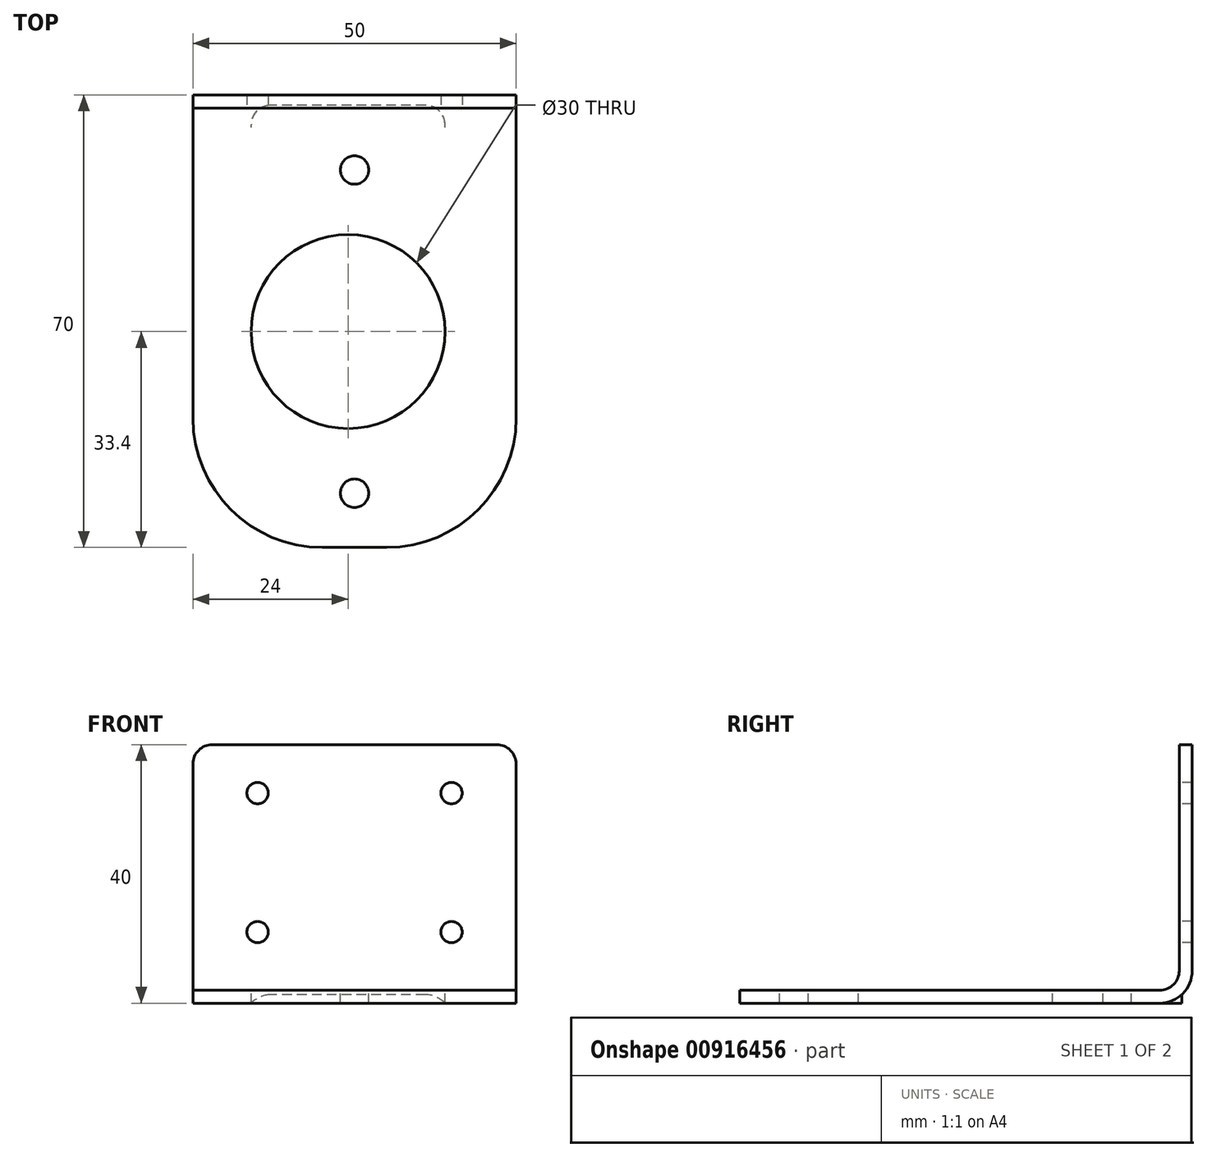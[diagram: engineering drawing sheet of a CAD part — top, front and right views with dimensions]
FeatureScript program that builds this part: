
annotation { "Feature Type Name" : "Feature", "Feature Type Description" : "" }
export const myFeature = defineFeature(function(context is Context, id is Id, definition is map)
    precondition{}
    {
        {
            var Q0;
            Q0=qCreatedBy(makeId("Right.planeOp"),FACE);
            var sketch = newSketch(context, id + "F0", { "sketchPlane" : qUnion([Q0])});
            skLineSegment(sketch, "E0", {"start": v(0, 5) * mm, "end": v(0, 40) * mm});
            skLineSegment(sketch, "E1", {"start": v(-5, 0) * mm, "end": v(-70, 0) * mm});
            skPoint(sketch, "E2.visualSharp", {"position": v(0, 0) * mm});
            skArc(sketch, "E2.filletArc", {"start": v(-5, 0) * mm, "mid": v(-1.46, 1.46) * mm, "end": v(0, 5) * mm});
            skLineSegment(sketch, "E3.0", {"start": v(-2, 5) * mm, "end": v(-2, 40) * mm});
            skArc(sketch, "E3.1", {"start": v(-5, 2) * mm, "mid": v(-2.88, 2.88) * mm, "end": v(-2, 5) * mm});
            skLineSegment(sketch, "E3.2", {"start": v(-5, 2) * mm, "end": v(-70, 2) * mm});
            skLineSegment(sketch, "E4", {"start": v(-70, 2) * mm, "end": v(-70, 0) * mm});
            skLineSegment(sketch, "E5", {"start": v(-2, 40) * mm, "end": v(0, 40) * mm});
            skSolve(sketch);
        }
        {
            var Q0;
            Q0=makeQuery(id+"F0.imprint","IMPRINT",FACE,{"disambiguationData":[TD([[makeQuery(id+"F0.imprint","IMPRINT",EDGE,{"derivedFrom":sQuery(id+"F0.wireOp",EDGE,"E0")}),1.0]])]});
            extrude(context, id + "F1", {"entities" : qUnion([Q0]), "endBound" : BoundingType.SYMMETRIC, "depth" : 50 * mm});
        }
        {
            var Q0;
            Q0=makeQuery(id+"F1.opExtrude","SWEPT_FACE",FACE,{"disambiguationData":[OSD([sQuery(id+"F0.wireOp",EDGE,"E3.0")])]});
            var sketch = newSketch(context, id + "F2", { "sketchPlane" : qUnion([Q0])});
            skLineSegment(sketch, "E6.bottom", {"start": v(15, 32.5) * mm, "end": v(-15, 32.5) * mm});
            skLineSegment(sketch, "E6.top", {"start": v(15, 11) * mm, "end": v(-15, 11) * mm});
            skLineSegment(sketch, "E6.left", {"start": v(15, 32.5) * mm, "end": v(15, 11) * mm});
            skLineSegment(sketch, "E6.right", {"start": v(-15, 32.5) * mm, "end": v(-15, 11) * mm});
            skPoint(sketch, "E6.middle", {"position": v(0, 21.75) * mm});
            skSolve(sketch);
        }
        {
            var Q0;
            Q0=sQuery(id+"F2.wireOp",VERTEX,"E6.right.start");
            var Q1;
            Q1=sQuery(id+"F2.wireOp",VERTEX,"E6.top.end");
            var Q2;
            Q2=sQuery(id+"F2.wireOp",VERTEX,"E6.left.end");
            var Q3;
            Q3=sQuery(id+"F2.wireOp",VERTEX,"E6.left.start");
            var Q4;
            Q4=makeQuery(id+"F1.opExtrude","SWEPT_BODY",BODY,{"disambiguationData":[OSD([sQuery(id+"F0.wireOp",EDGE,"E0"),sQuery(id+"F0.wireOp",EDGE,"E1"),sQuery(id+"F0.wireOp",EDGE,"E2.filletArc"),sQuery(id+"F0.wireOp",EDGE,"E3.0"),sQuery(id+"F0.wireOp",EDGE,"E3.1"),sQuery(id+"F0.wireOp",EDGE,"E3.2"),sQuery(id+"F0.wireOp",EDGE,"E4"),sQuery(id+"F0.wireOp",EDGE,"E5")])]});
            hole(context, id + "F3", {"style" : HoleStyle.SIMPLE, "endStyle" : HoleEndStyle.THROUGH, "standardTappedOrClearance" : lookupTablePath({ "standard" : "ISO", "fit" : "Normal", "size" : "M3", "type" : "Clearance" }), "standardBlindInLast" : lookupTablePath({ "fit" : "Standard", "standard" : "ISO", "size" : "M3", "type" : "Clearance" }), "holeDiameter" : 3.3 * mm, "tappedDepth" : 12 * mm, "tapClearance" : 3, "locations" : qUnion([Q0, Q1, Q2, Q3]), "scope" : qUnion([Q4])});
        }
        {
            var Q0;
            Q0=makeQuery(id+"F1.opExtrude","SWEPT_FACE",FACE,{"disambiguationData":[OSD([sQuery(id+"F0.wireOp",EDGE,"E3.2")])]});
            var sketch = newSketch(context, id + "F4", { "sketchPlane" : qUnion([Q0])});
            skLineSegment(sketch, "E7.bottom", {"start": v(14, -61.6) * mm, "end": v(14, -71.6) * mm});
            skLineSegment(sketch, "E7.top", {"start": v(-16, -61.6) * mm, "end": v(-16, -71.6) * mm});
            skLineSegment(sketch, "E7.left", {"start": v(14, -61.6) * mm, "end": v(-16, -61.6) * mm});
            skLineSegment(sketch, "E7.right", {"start": v(14, -68.4) * mm, "end": v(-16, -68.4) * mm});
            skLineSegment(sketch, "E8", {"start": v(0, -61.6) * mm, "end": v(0, -71.6) * mm, "construction": true});
            skLineSegment(sketch, "E9.MirrorCS", {"start": v(14, -11.6) * mm, "end": v(14, -1.6) * mm});
            skLineSegment(sketch, "E10.MirrorCS", {"start": v(-16, -11.6) * mm, "end": v(-16, -1.6) * mm});
            skLineSegment(sketch, "E11.MirrorCS", {"start": v(14, -11.6) * mm, "end": v(-16, -11.6) * mm});
            skLineSegment(sketch, "E12.MirrorCS", {"start": v(14, -1.6) * mm, "end": v(-16, -1.6) * mm});
            skLineSegment(sketch, "E13.MirrorCS", {"start": v(0, -11.6) * mm, "end": v(0, -1.6) * mm, "construction": true});
            skCircle(sketch, "E14", {"center": v(-1, -36.6) * mm, "radius": 15 * mm});
            skLineSegment(sketch, "E15", {"start": v(0, -21.63) * mm, "end": v(25, -21.63) * mm});
            skLineSegment(sketch, "E16", {"start": v(0, -51.57) * mm, "end": v(25, -51.57) * mm});
            skSolve(sketch);
        }
        {
            var Q0;
            Q0=makeQuery(id+"F4.imprint","IMPRINT",FACE,{"disambiguationData":[TD([[makeQuery(id+"F4.imprint","IMPRINT",EDGE,{"derivedFrom":sQuery(id+"F4.wireOp",EDGE,"E7.bottom")}),-1.0]])]});
            var Q1;
            Q1=makeQuery(id+"F4.imprint","IMPRINT",FACE,{"disambiguationData":[TD([[makeQuery(id+"F4.imprint","IMPRINT",EDGE,{"derivedFrom":sQuery(id+"F4.wireOp",EDGE,"E9.MirrorCS")}),1.0]])]});
            var Q2;
            Q2=makeQuery(id+"F1.opExtrude","SWEPT_FACE",FACE,{"disambiguationData":[OSD([sQuery(id+"F0.wireOp",EDGE,"E1")])]});
            extrude(context, id + "F5", {"entities" : qUnion([Q0, Q1]), "operationType" : NewBodyOperationType.ADD, "endBound" : BoundingType.UP_TO_SURFACE, "oppositeDirection" : true, "endBoundEntityFace" : qUnion([Q2]), "depth" : 25 * mm});
        }
        {
            var Q0;
            Q0=sQuery(id+"F4.wireOp",VERTEX,"E8.start");
            var Q1;
            Q1=sQuery(id+"F4.wireOp",VERTEX,"E13.MirrorCS.start");
            var Q2;
            Q2=makeQuery(id+"F1.opExtrude","SWEPT_BODY",BODY,{"disambiguationData":[OSD([sQuery(id+"F0.wireOp",EDGE,"E0"),sQuery(id+"F0.wireOp",EDGE,"E1"),sQuery(id+"F0.wireOp",EDGE,"E2.filletArc"),sQuery(id+"F0.wireOp",EDGE,"E3.0"),sQuery(id+"F0.wireOp",EDGE,"E3.1"),sQuery(id+"F0.wireOp",EDGE,"E3.2"),sQuery(id+"F0.wireOp",EDGE,"E4"),sQuery(id+"F0.wireOp",EDGE,"E5")])]});
            hole(context, id + "F6", {"style" : HoleStyle.SIMPLE, "endStyle" : HoleEndStyle.THROUGH, "standardTappedOrClearance" : lookupTablePath({ "standard" : "ISO", "fit" : "Normal", "size" : "M4", "type" : "Clearance" }), "standardBlindInLast" : lookupTablePath({ "fit" : "Standard", "standard" : "ISO", "size" : "M4", "type" : "Clearance" }), "holeDiameter" : 4.4 * mm, "tappedDepth" : 12 * mm, "tapClearance" : 3, "locations" : qUnion([Q0, Q1]), "scope" : qUnion([Q2])});
        }
        {
            var Q0;
            {var subQ0=sQuery(id+"F4.wireOp",EDGE,"hzME8n18-MPXb-ktXV-Iea0-p6DPRJ7Zrk4K");Q0=makeQuery(id+"F4.imprint","IMPRINT",FACE,{"disambiguationData":[TD([[makeQuery(id+"F4.imprint","IMPRINT",EDGE,{"derivedFrom":subQ0}),1.0]])]});}
            var Q1;
            {var subQ0=sQuery(id+"F4.wireOp",EDGE,"ZWVXp8VA-qsCd-atnR-KfRt-9iqPWuk9H4GU");Q1=makeQuery(id+"F4.imprint","IMPRINT",FACE,{"disambiguationData":[TD([[makeQuery(id+"F4.imprint","IMPRINT",EDGE,{"derivedFrom":subQ0}),-1.0]])]});}
            var Q2;
            {var subQ0=sQuery(id+"F4.wireOp",EDGE,"E14");var subQ1=makeQuery(id+"F4.imprint","INTERSECT",VERTEX,{"derivedFrom":[subQ0,sQuery(id+"F4.wireOp",EDGE,"E15")]});Q2=makeQuery(id+"F4.imprint","IMPRINT",FACE,{"disambiguationData":[TD([[makeQuery(id+"F4.imprint","IMPRINT",EDGE,{"disambiguationData":[TD([[subQ1,1.0]])],"derivedFrom":subQ0}),1.0]])]});}
            extrude(context, id + "F7", {"entities" : qUnion([Q0, Q1, Q2]), "operationType" : NewBodyOperationType.REMOVE, "endBound" : BoundingType.UP_TO_NEXT, "oppositeDirection" : true, "offsetDistance" : 25 * mm, "depth" : 25 * mm});
        }
        {
            var Q0;
            Q0=makeQuery(id+"F7.boolean.opBoolean","COPY",EDGE,{"derivedFrom":makeQuery(id+"F7.opExtrude","SWEPT_EDGE",EDGE,{"disambiguationData":[OSD([sQuery(id+"F0.wireOp",EDGE,"E3.2"),sQuery(id+"F0.wireOp",EDGE,"E4"),sQuery(id+"F4.wireOp",EDGE,"hzME8n18-MPXb-ktXV-Iea0-p6DPRJ7Zrk4K")])]})});
            var Q1;
            Q1=makeQuery(id+"F5.opExtrude","SWEPT_EDGE",EDGE,{"disambiguationData":[OSD([sQuery(id+"F4.wireOp",EDGE,"E7.bottom"),sQuery(id+"F4.wireOp",EDGE,"E7.right")])]});
            var Q2;
            Q2=makeQuery(id+"F5.opExtrude","SWEPT_EDGE",EDGE,{"disambiguationData":[OSD([sQuery(id+"F4.wireOp",EDGE,"E7.top"),sQuery(id+"F4.wireOp",EDGE,"E7.right")])]});
            var Q3;
            Q3=makeQuery(id+"F5.opExtrude","SWEPT_EDGE",EDGE,{"disambiguationData":[OSD([sQuery(id+"F0.wireOp",EDGE,"E3.2"),sQuery(id+"F4.wireOp",EDGE,"E7.top"),sQuery(id+"F4.wireOp",EDGE,"E7.left")])]});
            var Q4;
            Q4=makeQuery(id+"F1.opExtrude","CAP_EDGE",EDGE,{"disambiguationData":[OSD([sQuery(id+"F0.wireOp",EDGE,"E5")])],"isStart":true});
            var Q5;
            Q5=makeQuery(id+"F7.boolean.opBoolean","COPY",EDGE,{"derivedFrom":makeQuery(id+"F7.opExtrude","SWEPT_EDGE",EDGE,{"disambiguationData":[OSD([sQuery(id+"F0.wireOp",EDGE,"E3.2"),sQuery(id+"F0.wireOp",EDGE,"E4"),sQuery(id+"F4.wireOp",EDGE,"ZWVXp8VA-qsCd-atnR-KfRt-9iqPWuk9H4GU")])]})});
            var Q6;
            Q6=makeQuery(id+"F5.opExtrude","SWEPT_EDGE",EDGE,{"disambiguationData":[OSD([sQuery(id+"F4.wireOp",EDGE,"E9.MirrorCS"),sQuery(id+"F4.wireOp",EDGE,"E12.MirrorCS")])]});
            var Q7;
            Q7=makeQuery(id+"F5.opExtrude","SWEPT_EDGE",EDGE,{"disambiguationData":[OSD([sQuery(id+"F4.wireOp",EDGE,"E10.MirrorCS"),sQuery(id+"F4.wireOp",EDGE,"E12.MirrorCS")])]});
            var Q8;
            Q8=makeQuery(id+"F5.opExtrude","SWEPT_EDGE",EDGE,{"disambiguationData":[OSD([sQuery(id+"F0.wireOp",EDGE,"E3.2"),sQuery(id+"F4.wireOp",EDGE,"E10.MirrorCS"),sQuery(id+"F4.wireOp",EDGE,"E11.MirrorCS")])]});
            var Q9;
            Q9=makeQuery(id+"F1.opExtrude","CAP_EDGE",EDGE,{"disambiguationData":[OSD([sQuery(id+"F0.wireOp",EDGE,"E5")])],"isStart":false});
            fillet(context, id + "F8", {"entities" : qUnion([Q0, Q1, Q2, Q3, Q4, Q5, Q6, Q7, Q8, Q9]), "radius" : 3 * mm, "tangentPropagation" : true, "allowEdgeOverflow" : false});
        }
        {
            var Q0;
            Q0=makeQuery(id+"F1.opExtrude","CAP_EDGE",EDGE,{"disambiguationData":[OSD([sQuery(id+"F0.wireOp",EDGE,"E4")])],"isStart":true});
            var Q1;
            Q1=makeQuery(id+"F1.opExtrude","CAP_EDGE",EDGE,{"disambiguationData":[OSD([sQuery(id+"F0.wireOp",EDGE,"E4")])],"isStart":false});
            fillet(context, id + "F9", {"entities" : qUnion([Q0, Q1]), "radius" : 20 * mm, "tangentPropagation" : true, "allowEdgeOverflow" : false});
        }
    });
